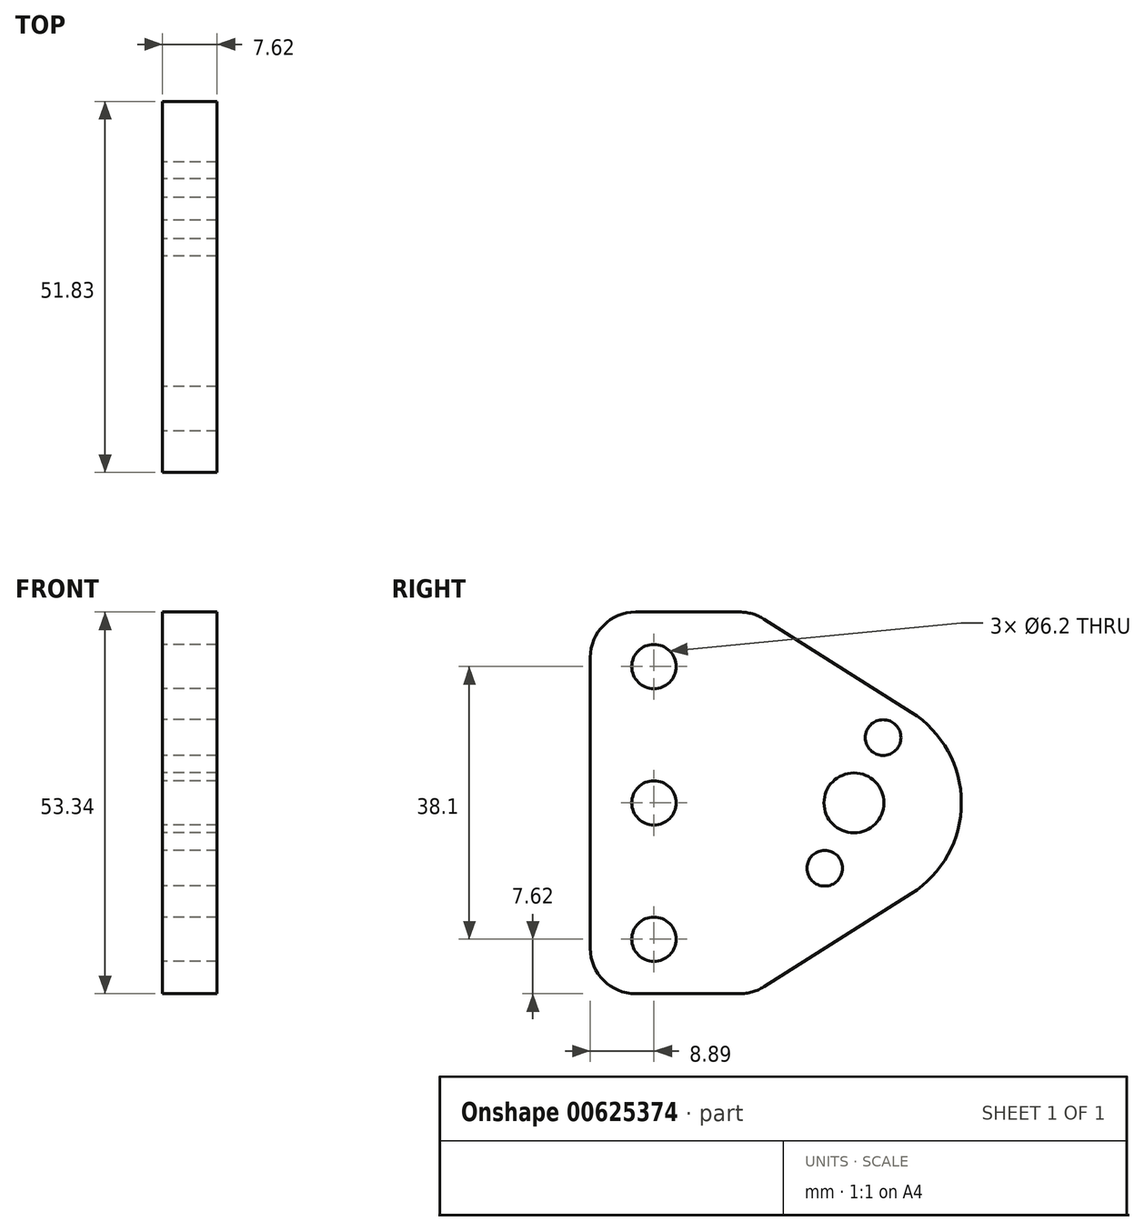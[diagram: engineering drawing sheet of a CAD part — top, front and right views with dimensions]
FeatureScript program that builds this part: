
annotation { "Feature Type Name" : "Feature", "Feature Type Description" : "" }
export const myFeature = defineFeature(function(context is Context, id is Id, definition is map)
    precondition{}
    {
        {
            var Q0;
            Q0=qCreatedBy(makeId("Right.planeOp"),FACE);
            var sketch = newSketch(context, id + "F0", { "sketchPlane" : qUnion([Q0])});
            skCircle(sketch, "E0", {"center": v(0, 0) * mm, "radius": 3.1 * mm});
            skCircle(sketch, "E1", {"center": v(0, 19.05) * mm, "radius": 3.1 * mm});
            skLineSegment(sketch, "E2.bottom", {"start": v(-8.9, 26.67) * mm, "end": v(13.82, 26.67) * mm});
            skLineSegment(sketch, "E2.top", {"start": v(-8.89, -26.67) * mm, "end": v(13.82, -26.67) * mm});
            skLineSegment(sketch, "E2.left", {"start": v(-8.9, 26.67) * mm, "end": v(-8.89, -26.67) * mm});
            skLineSegment(sketch, "E3", {"start": v(0, 0) * mm, "end": v(-8.89, 0) * mm, "construction": true});
            skCircle(sketch, "E4.MirrorC", {"center": v(0, -19.05) * mm, "radius": 3.1 * mm});
            skCircle(sketch, "E5", {"center": v(27.94, 0) * mm, "radius": 4.2 * mm});
            skCircle(sketch, "E6", {"center": v(27.94, 0) * mm, "radius": 15 * mm, "construction": true});
            skLineSegment(sketch, "E7", {"start": v(10, 32.15) * mm, "end": v(10, -40.6) * mm, "construction": true});
            skArc(sketch, "E8", {"start": v(35.95, -12.68) * mm, "mid": v(42.94, 0) * mm, "end": v(35.95, 12.68) * mm});
            skLineSegment(sketch, "E9", {"start": v(13.82, 26.67) * mm, "end": v(35.95, 12.68) * mm});
            skLineSegment(sketch, "E10", {"start": v(35.95, -12.68) * mm, "end": v(13.82, -26.67) * mm});
            skCircle(sketch, "E11", {"center": v(32.02, 9.13) * mm, "radius": 2.49 * mm});
            skCircle(sketch, "E12", {"center": v(23.86, -9.13) * mm, "radius": 2.49 * mm});
            skLineSegment(sketch, "E13", {"start": v(32.02, 9.13) * mm, "end": v(23.86, -9.13) * mm, "construction": true});
            skSolve(sketch);
        }
        {
            var Q0;
            Q0 = qSketchRegion(id + "F0", true);
            extrude(context, id + "F1", {"entities" : qUnion([Q0]), "endBound" : BoundingType.SYMMETRIC, "depth" : 7.62 * mm, "offsetDistance" : 25.4 * mm});
        }
        {
            var Q0;
            Q0=makeQuery(id+"F1.opExtrude","SWEPT_EDGE",EDGE,{"disambiguationData":[OSD([sQuery(id+"F0.wireOp",EDGE,"E2.bottom"),sQuery(id+"F0.wireOp",EDGE,"E2.left")])]});
            var Q1;
            Q1=makeQuery(id+"F1.opExtrude","SWEPT_EDGE",EDGE,{"disambiguationData":[OSD([sQuery(id+"F0.wireOp",EDGE,"E2.bottom"),sQuery(id+"F0.wireOp",EDGE,"E9")])]});
            var Q2;
            Q2=makeQuery(id+"F1.opExtrude","SWEPT_EDGE",EDGE,{"disambiguationData":[OSD([sQuery(id+"F0.wireOp",EDGE,"E2.top"),sQuery(id+"F0.wireOp",EDGE,"E2.left")])]});
            var Q3;
            Q3=makeQuery(id+"F1.opExtrude","SWEPT_EDGE",EDGE,{"disambiguationData":[OSD([sQuery(id+"F0.wireOp",EDGE,"E2.top"),sQuery(id+"F0.wireOp",EDGE,"E10")])]});
            fillet(context, id + "F2", {"entities" : qUnion([Q0, Q1, Q2, Q3]), "radius" : 6.35 * mm, "tangentPropagation" : true, "allowEdgeOverflow" : false});
        }
    });
